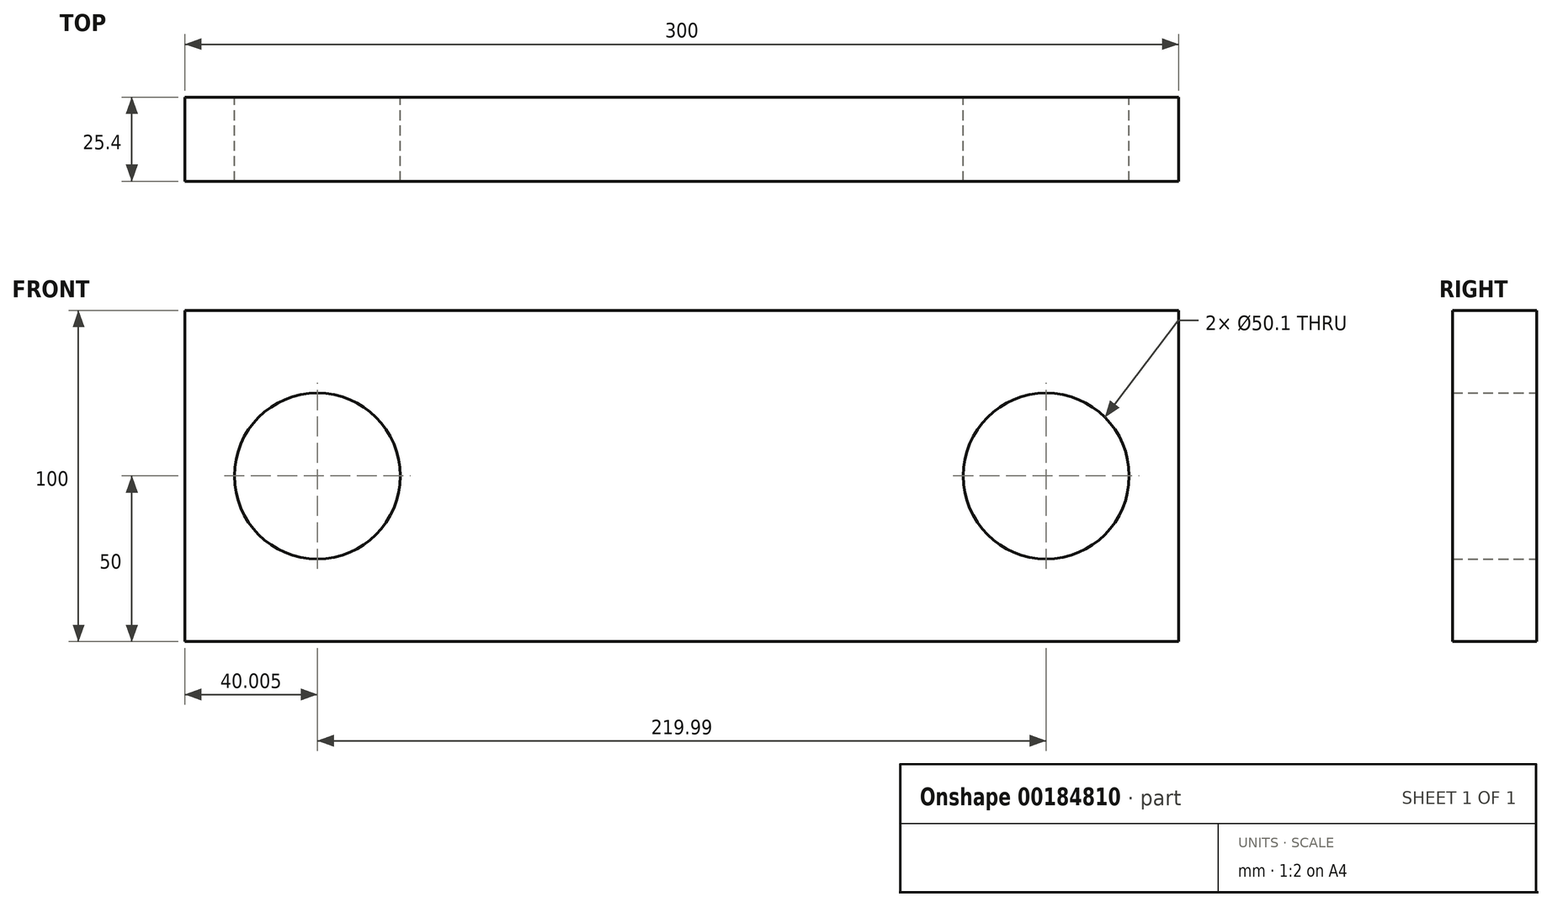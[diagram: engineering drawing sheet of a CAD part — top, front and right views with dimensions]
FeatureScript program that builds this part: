
annotation { "Feature Type Name" : "Feature", "Feature Type Description" : "" }
export const myFeature = defineFeature(function(context is Context, id is Id, definition is map)
    precondition{}
    {
        {
            var Q0;
            Q0=qCreatedBy(makeId("Front.planeOp"),FACE);
            var sketch = newSketch(context, id + "F0", { "sketchPlane" : qUnion([Q0])});
            skLineSegment(sketch, "E0.bottom", {"start": v(0, 0) * mm, "end": v(300, 0) * mm});
            skLineSegment(sketch, "E0.top", {"start": v(0, 100) * mm, "end": v(300, 100) * mm});
            skLineSegment(sketch, "E0.left", {"start": v(0, 0) * mm, "end": v(0, 100) * mm});
            skLineSegment(sketch, "E0.right", {"start": v(300, 0) * mm, "end": v(300, 100) * mm});
            skLineSegment(sketch, "E1", {"start": v(0, 50) * mm, "end": v(40, 50) * mm, "construction": true});
            skCircle(sketch, "E2", {"center": v(40, 50) * mm, "radius": 25.05 * mm});
            skLineSegment(sketch, "E3", {"start": v(300, 50) * mm, "end": v(260, 50) * mm, "construction": true});
            skCircle(sketch, "E4", {"center": v(260, 50) * mm, "radius": 25.05 * mm});
            skSolve(sketch);
        }
        {
            var Q0;
            Q0=makeQuery(id+"F0.imprint","IMPRINT",FACE,{"disambiguationData":[TD([[makeQuery(id+"F0.imprint","IMPRINT",EDGE,{"derivedFrom":sQuery(id+"F0.wireOp",EDGE,"E0.bottom")}),1.0]])]});
            extrude(context, id + "F1", {"entities" : qUnion([Q0]), "depth" : 25.4 * mm});
        }
    });
